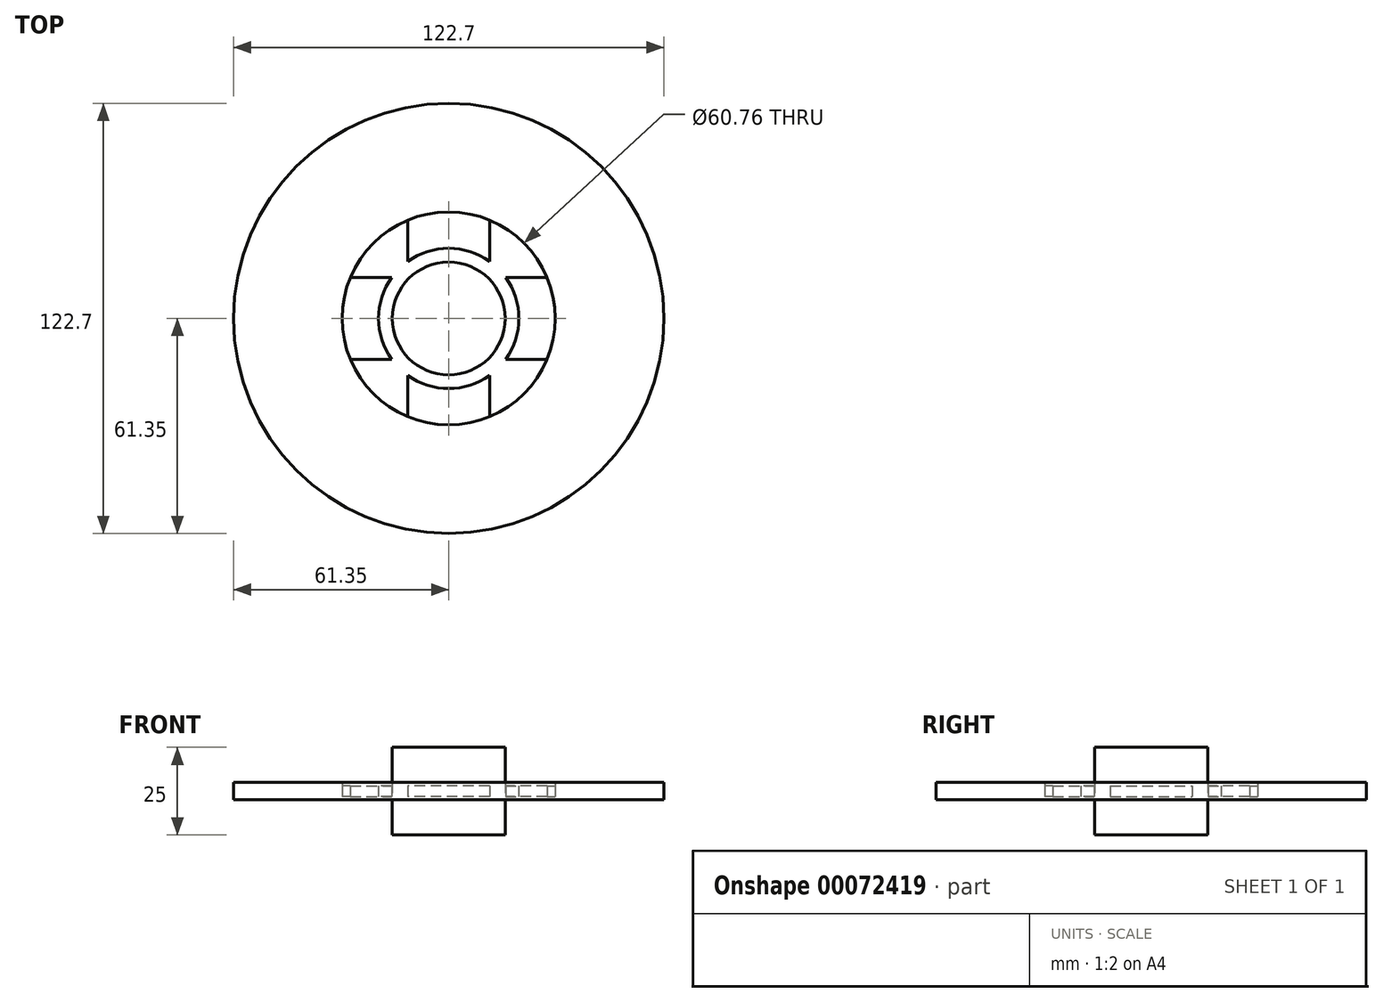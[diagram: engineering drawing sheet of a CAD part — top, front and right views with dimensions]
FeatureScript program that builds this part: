
annotation { "Feature Type Name" : "Feature", "Feature Type Description" : "" }
export const myFeature = defineFeature(function(context is Context, id is Id, definition is map)
    precondition{}
    {
        {
            var Q0;
            Q0=qCreatedBy(makeId("Top.planeOp"),FACE);
            var sketch = newSketch(context, id + "F0", { "sketchPlane" : qUnion([Q0])});
            skCircle(sketch, "E0", {"center": v(0, 0) * mm, "radius": 61.35 * mm});
            skCircle(sketch, "E1", {"center": v(0, 0) * mm, "radius": 30.38 * mm});
            skCircle(sketch, "E2", {"center": v(0, 0) * mm, "radius": 20 * mm});
            skLineSegment(sketch, "E3", {"start": v(-11.67, 60.23) * mm, "end": v(-11.67, 16.24) * mm});
            skLineSegment(sketch, "E4.MirrorCS", {"start": v(11.67, 60.23) * mm, "end": v(11.67, 16.24) * mm});
            skLineSegment(sketch, "E5.1.0", {"start": v(-60.23, -11.67) * mm, "end": v(-16.24, -11.67) * mm});
            skLineSegment(sketch, "E5.1.1", {"start": v(-60.23, 11.67) * mm, "end": v(-16.24, 11.67) * mm});
            skLineSegment(sketch, "E5.2.0", {"start": v(11.67, -60.23) * mm, "end": v(11.67, -16.24) * mm});
            skLineSegment(sketch, "E5.2.1", {"start": v(-11.67, -60.23) * mm, "end": v(-11.67, -16.24) * mm});
            skLineSegment(sketch, "E5.3.0", {"start": v(60.23, 11.67) * mm, "end": v(16.24, 11.67) * mm});
            skLineSegment(sketch, "E5.3.1", {"start": v(60.23, -11.67) * mm, "end": v(16.24, -11.67) * mm});
            skPoint(sketch, "E6.orphan", {"position": v(-11.67, 28.05) * mm});
            skPoint(sketch, "E7.orphan", {"position": v(11.67, 28.05) * mm});
            skPoint(sketch, "E8.orphan", {"position": v(28.05, 11.67) * mm});
            skPoint(sketch, "E9.orphan", {"position": v(28.05, -11.67) * mm});
            skPoint(sketch, "E10.orphan", {"position": v(11.67, -28.05) * mm});
            skPoint(sketch, "E11.orphan", {"position": v(-11.67, -28.05) * mm});
            skPoint(sketch, "E12.orphan", {"position": v(-28.05, -11.67) * mm});
            skPoint(sketch, "E13.orphan", {"position": v(-28.05, 11.67) * mm});
            skCircle(sketch, "E14", {"center": v(0, 0) * mm, "radius": 16.09 * mm});
            skSolve(sketch);
        }
        {
            var Q0;
            {var subQ0=sQuery(id+"F0.wireOp",EDGE,"E5.1.0");var subQ1=sQuery(id+"F0.wireOp",EDGE,"E0");var subQ2=makeQuery(id+"F0.imprint","INTERSECT",VERTEX,{"derivedFrom":[subQ1,subQ0]});Q0=makeQuery(id+"F0.imprint","IMPRINT",FACE,{"disambiguationData":[TD([[makeQuery(id+"F0.imprint","IMPRINT",EDGE,{"disambiguationData":[TD([[subQ2,-1.0]])],"derivedFrom":subQ1}),1.0]])]});}
            var Q1;
            {var subQ0=sQuery(id+"F0.wireOp",EDGE,"E5.1.0");var subQ1=sQuery(id+"F0.wireOp",EDGE,"E0");var subQ2=makeQuery(id+"F0.imprint","INTERSECT",VERTEX,{"derivedFrom":[subQ1,subQ0]});Q1=makeQuery(id+"F0.imprint","IMPRINT",FACE,{"disambiguationData":[TD([[makeQuery(id+"F0.imprint","IMPRINT",EDGE,{"disambiguationData":[TD([[subQ2,1.0]])],"derivedFrom":subQ1}),1.0]])]});}
            var Q2;
            {var subQ0=sQuery(id+"F0.wireOp",EDGE,"E3");var subQ1=sQuery(id+"F0.wireOp",EDGE,"E0");var subQ2=makeQuery(id+"F0.imprint","INTERSECT",VERTEX,{"derivedFrom":[subQ1,subQ0]});Q2=makeQuery(id+"F0.imprint","IMPRINT",FACE,{"disambiguationData":[TD([[makeQuery(id+"F0.imprint","IMPRINT",EDGE,{"disambiguationData":[TD([[subQ2,-1.0]])],"derivedFrom":subQ1}),1.0]])]});}
            var Q3;
            {var subQ0=sQuery(id+"F0.wireOp",EDGE,"E3");var subQ1=sQuery(id+"F0.wireOp",EDGE,"E0");var subQ2=makeQuery(id+"F0.imprint","INTERSECT",VERTEX,{"derivedFrom":[subQ1,subQ0]});Q3=makeQuery(id+"F0.imprint","IMPRINT",FACE,{"disambiguationData":[TD([[makeQuery(id+"F0.imprint","IMPRINT",EDGE,{"disambiguationData":[TD([[subQ2,1.0]])],"derivedFrom":subQ1}),1.0]])]});}
            var Q4;
            {var subQ0=sQuery(id+"F0.wireOp",EDGE,"E4.MirrorCS");var subQ1=sQuery(id+"F0.wireOp",EDGE,"E0");var subQ2=makeQuery(id+"F0.imprint","INTERSECT",VERTEX,{"derivedFrom":[subQ1,subQ0]});Q4=makeQuery(id+"F0.imprint","IMPRINT",FACE,{"disambiguationData":[TD([[makeQuery(id+"F0.imprint","IMPRINT",EDGE,{"disambiguationData":[TD([[subQ2,1.0]])],"derivedFrom":subQ1}),1.0]])]});}
            var Q5;
            {var subQ0=sQuery(id+"F0.wireOp",EDGE,"E5.3.0");var subQ1=sQuery(id+"F0.wireOp",EDGE,"E0");var subQ2=makeQuery(id+"F0.imprint","INTERSECT",VERTEX,{"derivedFrom":[subQ1,subQ0]});Q5=makeQuery(id+"F0.imprint","IMPRINT",FACE,{"disambiguationData":[TD([[makeQuery(id+"F0.imprint","IMPRINT",EDGE,{"disambiguationData":[TD([[subQ2,1.0]])],"derivedFrom":subQ1}),1.0]])]});}
            var Q6;
            {var subQ0=sQuery(id+"F0.wireOp",EDGE,"E5.2.0");var subQ1=sQuery(id+"F0.wireOp",EDGE,"E0");var subQ2=makeQuery(id+"F0.imprint","INTERSECT",VERTEX,{"derivedFrom":[subQ1,subQ0]});Q6=makeQuery(id+"F0.imprint","IMPRINT",FACE,{"disambiguationData":[TD([[makeQuery(id+"F0.imprint","IMPRINT",EDGE,{"disambiguationData":[TD([[subQ2,-1.0]])],"derivedFrom":subQ1}),1.0]])]});}
            var Q7;
            {var subQ0=sQuery(id+"F0.wireOp",EDGE,"E5.2.0");var subQ1=sQuery(id+"F0.wireOp",EDGE,"E0");var subQ2=makeQuery(id+"F0.imprint","INTERSECT",VERTEX,{"derivedFrom":[subQ1,subQ0]});Q7=makeQuery(id+"F0.imprint","IMPRINT",FACE,{"disambiguationData":[TD([[makeQuery(id+"F0.imprint","IMPRINT",EDGE,{"disambiguationData":[TD([[subQ2,1.0]])],"derivedFrom":subQ1}),1.0]])]});}
            extrude(context, id + "F1", {"entities" : qUnion([Q0, Q1, Q2, Q3, Q4, Q5, Q6, Q7]), "endBound" : BoundingType.SYMMETRIC, "depth" : 5 * mm});
        }
        {
            var Q0;
            {var subQ0=sQuery(id+"F0.wireOp",EDGE,"E5.1.1");var subQ1=sQuery(id+"F0.wireOp",EDGE,"E1");var subQ2=makeQuery(id+"F0.imprint","INTERSECT",VERTEX,{"derivedFrom":[subQ1,subQ0]});Q0=makeQuery(id+"F0.imprint","IMPRINT",FACE,{"disambiguationData":[TD([[makeQuery(id+"F0.imprint","IMPRINT",EDGE,{"disambiguationData":[TD([[subQ2,-1.0]])],"derivedFrom":subQ1}),1.0]])]});}
            var Q1;
            {var subQ0=sQuery(id+"F0.wireOp",EDGE,"E4.MirrorCS");var subQ1=sQuery(id+"F0.wireOp",EDGE,"E1");var subQ2=makeQuery(id+"F0.imprint","INTERSECT",VERTEX,{"derivedFrom":[subQ1,subQ0]});Q1=makeQuery(id+"F0.imprint","IMPRINT",FACE,{"disambiguationData":[TD([[makeQuery(id+"F0.imprint","IMPRINT",EDGE,{"disambiguationData":[TD([[subQ2,-1.0]])],"derivedFrom":subQ1}),1.0]])]});}
            var Q2;
            {var subQ0=sQuery(id+"F0.wireOp",EDGE,"E5.3.0");var subQ1=sQuery(id+"F0.wireOp",EDGE,"E1");var subQ2=makeQuery(id+"F0.imprint","INTERSECT",VERTEX,{"derivedFrom":[subQ1,subQ0]});Q2=makeQuery(id+"F0.imprint","IMPRINT",FACE,{"disambiguationData":[TD([[makeQuery(id+"F0.imprint","IMPRINT",EDGE,{"disambiguationData":[TD([[subQ2,1.0]])],"derivedFrom":subQ1}),1.0]])]});}
            var Q3;
            {var subQ0=sQuery(id+"F0.wireOp",EDGE,"E5.2.1");var subQ1=sQuery(id+"F0.wireOp",EDGE,"E1");var subQ2=makeQuery(id+"F0.imprint","INTERSECT",VERTEX,{"derivedFrom":[subQ1,subQ0]});Q3=makeQuery(id+"F0.imprint","IMPRINT",FACE,{"disambiguationData":[TD([[makeQuery(id+"F0.imprint","IMPRINT",EDGE,{"disambiguationData":[TD([[subQ2,-1.0]])],"derivedFrom":subQ1}),1.0]])]});}
            extrude(context, id + "F2", {"entities" : qUnion([Q0, Q1, Q2, Q3]), "endBound" : BoundingType.SYMMETRIC, "depth" : 3 * mm});
        }
        {
            var Q0;
            Q0=makeQuery(id+"F0.imprint","IMPRINT",FACE,{"disambiguationData":[TD([[makeQuery(id+"F0.imprint","IMPRINT",EDGE,{"derivedFrom":sQuery(id+"F0.wireOp",EDGE,"E14")}),1.0]])]});
            extrude(context, id + "F3", {"entities" : qUnion([Q0]), "endBound" : BoundingType.SYMMETRIC, "depth" : 25 * mm});
        }
    });
